# Revit family: ACM_57.71_Volume Control Damper_TVJ
name_source: partatom
category: Duct Accessories
revit_build: Autodesk Revit 2017 (Build: 20170816_0615(x64)
units: mm (PartAtom-declared; Revit-internal decimal feet)

## family parameters
Always vertical = Yes
Cut with Voids When Loaded = No
Part Type = Damper
Round Connector Dimension = Use Diameter
Shared = No
Work Plane-Based = No

## types (49) — shared parameters
ACM_MEP_Air Flow_Max = 0.0 L/s
ACM_MEP_Air Flow_Min = 0.0 L/s
ACM_MEP_Apparent Power = 0 VA
ACM_MEP_Elec. Frecuency = 0 Hz
ACM_MEP_Elec. Power = 0 W
ACM_MEP_Item Type = VCD
ACM_MEP_Number of Poles = 1
ACM_MEP_Pressure_Exhaust = 0.0 Pa
ACM_MEP_Pressure_Max = 0.0 Pa
ACM_MEP_Pressure_Min = 0.0 Pa
ACM_MEP_Pressure_Supply = 0.0 Pa
ACM_MEP_Velocity_Max = 0.0 m/s
ACM_MEP_Velocity_Min = 0.0 m/s
ACM_MEP_Voltage = 0 V
ACM_MEP_Weight = 0.00 kg
CAT0 = Yes
Description = VAV control units, supply/extract air, acoustic cladding
L = 400 mm  [stored 1.31234 ft]
L2 = 200 mm  [stored 0.656168 ft]
L2D = 400 mm  [stored 1.31234 ft]
Manufacturer = TROX
magiPartTypeId = 203
magiProductFamilyId = TVJD-*/*X*
zero-valued in all types: ACM_MEP_Length, ACM_MEP_Motor_Frecuency, ACM_MEP_Power Factor, MC_Default_elevation

## per-type parameters (varying)
| type | ACM_MEP_Connection_Diameter | ACM_MEP_Connection_Height | ACM_MEP_Connection_Width | ACM_MEP_Height | ACM_MEP_Number Type | ACM_MEP_Width | B | B22 | H | H22 | H2D | W2D | magiProductCode | magiProductId |
| 57.71_VCD_Volume Control Damper_TVJ_200X200 | 0 mm  [stored 0 ft] | 0 mm  [stored 0 ft] | 0 mm  [stored 0 ft] | 0 mm  [stored 0 ft] | 200mm x 200mm | 0 mm  [stored 0 ft] | 200 mm | 140 mm  [stored 0.459318 ft] | 200 mm | 140 mm  [stored 0.459318 ft] | 280 mm | 280 mm | TVJ-D/200X200 | TVJD-*/200X200 |
| 57.71_VCD_Volume Control Damper_TVJ_300X100 | 0 mm  [stored 0 ft] | 0 mm  [stored 0 ft] | 0 mm  [stored 0 ft] | 0 mm  [stored 0 ft] |  | 0 mm  [stored 0 ft] | 300 mm | 190 mm  [stored 0.62336 ft] | 100 mm | 90 mm  [stored 0.295276 ft] | 180 mm  [stored 0.590551 ft] | 380 mm | TVJ-D/300X100 | TVJD-*/300X100 |
| 57.71_VCD_Volume Control Damper_TVJ_300X200 | 0 mm  [stored 0 ft] | 0 mm  [stored 0 ft] | 0 mm  [stored 0 ft] | 0 mm  [stored 0 ft] | 300mm x 200mm | 0 mm  [stored 0 ft] | 300 mm | 190 mm  [stored 0.62336 ft] | 200 mm | 140 mm  [stored 0.459318 ft] | 280 mm | 380 mm | TVJ-D/300X200 | TVJD-*/300X200 |
| 57.71_VCD_Volume Control Damper_TVJ_300X300 | 0 mm  [stored 0 ft] | 0 mm  [stored 0 ft] | 0 mm  [stored 0 ft] | 0 mm  [stored 0 ft] | 300mm x 300mm | 0 mm  [stored 0 ft] | 300 mm | 190 mm  [stored 0.62336 ft] | 300 mm | 190 mm  [stored 0.62336 ft] | 380 mm | 380 mm | TVJ-D/300X300 | TVJD-*/300X300 |
| 57.71_VCD_Volume Control Damper_TVJ_400X100 | 0 mm  [stored 0 ft] | 0 mm  [stored 0 ft] | 0 mm  [stored 0 ft] | 0 mm  [stored 0 ft] |  | 0 mm  [stored 0 ft] | 400 mm | 240 mm  [stored 0.787402 ft] | 100 mm | 90 mm  [stored 0.295276 ft] | 180 mm  [stored 0.590551 ft] | 480 mm | TVJ-D/400X100 | TVJD-*/400X100 |
| 57.71_VCD_Volume Control Damper_TVJ_400X200 | 0 mm  [stored 0 ft] | 0 mm  [stored 0 ft] | 0 mm  [stored 0 ft] | 0 mm  [stored 0 ft] |  | 0 mm  [stored 0 ft] | 400 mm | 240 mm  [stored 0.787402 ft] | 200 mm | 140 mm  [stored 0.459318 ft] | 280 mm | 480 mm | TVJ-D/400X200 | TVJD-*/400X200 |
| 57.71_VCD_Volume Control Damper_TVJ_400X300 | 0 mm  [stored 0 ft] | 0 mm  [stored 0 ft] | 0 mm  [stored 0 ft] | 0 mm  [stored 0 ft] | 400mm x 300mm | 0 mm  [stored 0 ft] | 400 mm | 240 mm  [stored 0.787402 ft] | 300 mm | 190 mm  [stored 0.62336 ft] | 380 mm | 480 mm | TVJ-D/400X300 | TVJD-*/400X300 |
| 57.71_VCD_Volume Control Damper_TVJ_400X400 | 0 mm  [stored 0 ft] | 0 mm  [stored 0 ft] | 0 mm  [stored 0 ft] | 0 mm  [stored 0 ft] | 400mm x 400mm | 0 mm  [stored 0 ft] | 400 mm | 240 mm  [stored 0.787402 ft] | 400 mm | 240 mm  [stored 0.787402 ft] | 480 mm | 480 mm | TVJ-D/400X400 | TVJD-*/400X400 |
| 57.71_VCD_Volume Control Damper_TVJ_500X100 | 0 mm  [stored 0 ft] | 0 mm  [stored 0 ft] | 0 mm  [stored 0 ft] | 0 mm  [stored 0 ft] |  | 0 mm  [stored 0 ft] | 500 mm | 290 mm  [stored 0.951444 ft] | 100 mm | 90 mm  [stored 0.295276 ft] | 180 mm  [stored 0.590551 ft] | 580 mm | TVJ-D/500X100 | TVJD-*/500X100 |
| 57.71_VCD_Volume Control Damper_TVJ_500X200 | 0 mm  [stored 0 ft] | 0 mm  [stored 0 ft] | 0 mm  [stored 0 ft] | 0 mm  [stored 0 ft] |  | 0 mm  [stored 0 ft] | 500 mm | 290 mm  [stored 0.951444 ft] | 200 mm | 140 mm  [stored 0.459318 ft] | 280 mm | 580 mm | TVJ-D/500X200 | TVJD-*/500X200 |
| 57.71_VCD_Volume Control Damper_TVJ_500X300 | 0 mm  [stored 0 ft] | 0 mm  [stored 0 ft] | 0 mm  [stored 0 ft] | 0 mm  [stored 0 ft] | 500mm x 300mm | 0 mm  [stored 0 ft] | 500 mm | 290 mm  [stored 0.951444 ft] | 300 mm | 190 mm  [stored 0.62336 ft] | 380 mm | 580 mm | TVJ-D/500X300 | TVJD-*/500X300 |
| 57.71_VCD_Volume Control Damper_TVJ_500X400 | 0 mm  [stored 0 ft] | 0 mm  [stored 0 ft] | 0 mm  [stored 0 ft] | 0 mm  [stored 0 ft] | 500mm x 400mm | 0 mm  [stored 0 ft] | 500 mm | 290 mm  [stored 0.951444 ft] | 400 mm | 240 mm  [stored 0.787402 ft] | 480 mm | 580 mm | TVJ-D/500X400 | TVJD-*/500X400 |
| 57.71_VCD_Volume Control Damper_TVJ_500X500 | 0 mm  [stored 0 ft] | 0 mm  [stored 0 ft] | 0 mm  [stored 0 ft] | 0 mm  [stored 0 ft] |  | 0 mm  [stored 0 ft] | 500 mm | 290 mm  [stored 0.951444 ft] | 500 mm | 290 mm  [stored 0.951444 ft] | 580 mm | 580 mm | TVJ-D/500X500 | TVJD-*/500X500 |
| 57.71_VCD_Volume Control Damper_TVJ_600X100 | 0 mm  [stored 0 ft] | 0 mm  [stored 0 ft] | 0 mm  [stored 0 ft] | 0 mm  [stored 0 ft] |  | 0 mm  [stored 0 ft] | 600 mm | 340 mm  [stored 1.11549 ft] | 100 mm | 90 mm  [stored 0.295276 ft] | 180 mm  [stored 0.590551 ft] | 680 mm | TVJ-D/600X100 | TVJD-*/600X100 |
| 57.71_VCD_Volume Control Damper_TVJ_600X200 | 0 mm  [stored 0 ft] | 0 mm  [stored 0 ft] | 0 mm  [stored 0 ft] | 0 mm  [stored 0 ft] |  | 0 mm  [stored 0 ft] | 600 mm | 340 mm  [stored 1.11549 ft] | 200 mm | 140 mm  [stored 0.459318 ft] | 280 mm | 680 mm | TVJ-D/600X200 | TVJD-*/600X200 |
| 57.71_VCD_Volume Control Damper_TVJ_600X300 | 0 mm  [stored 0 ft] | 0 mm  [stored 0 ft] | 0 mm  [stored 0 ft] | 0 mm  [stored 0 ft] | 600mm x 300mm | 0 mm  [stored 0 ft] | 600 mm | 340 mm  [stored 1.11549 ft] | 300 mm | 190 mm  [stored 0.62336 ft] | 380 mm | 680 mm | TVJ-D/600X300 | TVJD-*/600X300 |
| 57.71_VCD_Volume Control Damper_TVJ_600X400 | 0 mm  [stored 0 ft] | 0 mm  [stored 0 ft] | 0 mm  [stored 0 ft] | 0 mm  [stored 0 ft] | 600mm x 400mm | 0 mm  [stored 0 ft] | 600 mm | 340 mm  [stored 1.11549 ft] | 400 mm | 240 mm  [stored 0.787402 ft] | 480 mm | 680 mm | TVJ-D/600X400 | TVJD-*/600X400 |
| 57.71_VCD_Volume Control Damper_TVJ_600X500 | 0 mm  [stored 0 ft] | 0 mm  [stored 0 ft] | 0 mm  [stored 0 ft] | 0 mm  [stored 0 ft] |  | 0 mm  [stored 0 ft] | 600 mm | 340 mm  [stored 1.11549 ft] | 500 mm | 290 mm  [stored 0.951444 ft] | 580 mm | 680 mm | TVJ-D/600X500 | TVJD-*/600X500 |
| 57.71_VCD_Volume Control Damper_TVJ_600X600 | 0 mm  [stored 0 ft] | 0 mm  [stored 0 ft] | 0 mm  [stored 0 ft] | 0 mm  [stored 0 ft] |  | 0 mm  [stored 0 ft] | 600 mm | 340 mm  [stored 1.11549 ft] | 600 mm | 340 mm  [stored 1.11549 ft] | 680 mm | 680 mm | TVJ-D/600X600 | TVJD-*/600X600 |
| 57.71_VCD_Volume Control Damper_TVJ_700X200 | 0 mm  [stored 0 ft] | 0 mm  [stored 0 ft] | 0 mm  [stored 0 ft] | 0 mm  [stored 0 ft] |  | 0 mm  [stored 0 ft] | 700 mm | 390 mm  [stored 1.27953 ft] | 200 mm | 140 mm  [stored 0.459318 ft] | 280 mm | 780 mm | TVJ-D/700X200 | TVJD-*/700X200 |
| 57.71_VCD_Volume Control Damper_TVJ_700X300 | 0 mm  [stored 0 ft] | 0 mm  [stored 0 ft] | 0 mm  [stored 0 ft] | 0 mm  [stored 0 ft] | 700mm x 300mm | 0 mm  [stored 0 ft] | 700 mm | 390 mm  [stored 1.27953 ft] | 300 mm | 190 mm  [stored 0.62336 ft] | 380 mm | 780 mm | TVJ-D/700X300 | TVJD-*/700X300 |
| 57.71_VCD_Volume Control Damper_TVJ_700X400 | 0 mm  [stored 0 ft] | 0 mm  [stored 0 ft] | 0 mm  [stored 0 ft] | 0 mm  [stored 0 ft] |  | 0 mm  [stored 0 ft] | 700 mm | 390 mm  [stored 1.27953 ft] | 400 mm | 240 mm  [stored 0.787402 ft] | 480 mm | 780 mm | TVJ-D/700X400 | TVJD-*/700X400 |
| 57.71_VCD_Volume Control Damper_TVJ_700X500 | 0 mm  [stored 0 ft] | 0 mm  [stored 0 ft] | 0 mm  [stored 0 ft] | 0 mm  [stored 0 ft] |  | 0 mm  [stored 0 ft] | 700 mm | 390 mm  [stored 1.27953 ft] | 500 mm | 290 mm  [stored 0.951444 ft] | 580 mm | 780 mm | TVJ-D/700X500 | TVJD-*/700X500 |
| 57.71_VCD_Volume Control Damper_TVJ_700X600 | 0 mm  [stored 0 ft] | 0 mm  [stored 0 ft] | 0 mm  [stored 0 ft] | 0 mm  [stored 0 ft] |  | 0 mm  [stored 0 ft] | 700 mm | 390 mm  [stored 1.27953 ft] | 600 mm | 340 mm  [stored 1.11549 ft] | 680 mm | 780 mm | TVJ-D/700X600 | TVJD-*/700X600 |
| 57.71_VCD_Volume Control Damper_TVJ_700X700 | 0 mm  [stored 0 ft] | 0 mm  [stored 0 ft] | 0 mm  [stored 0 ft] | 0 mm  [stored 0 ft] |  | 0 mm  [stored 0 ft] | 700 mm | 390 mm  [stored 1.27953 ft] | 700 mm | 390 mm  [stored 1.27953 ft] | 780 mm | 780 mm | TVJ-D/700X700 | TVJD-*/700X700 |
| 57.71_VCD_Volume Control Damper_TVJ_800X200 | 0 mm  [stored 0 ft] | 0 mm  [stored 0 ft] | 0 mm  [stored 0 ft] | 0 mm  [stored 0 ft] |  | 0 mm  [stored 0 ft] | 800 mm | 440 mm  [stored 1.44357 ft] | 200 mm | 140 mm  [stored 0.459318 ft] | 280 mm | 880 mm | TVJ-D/800X200 | TVJD-*/800X200 |
| 57.71_VCD_Volume Control Damper_TVJ_800X300 | 0 mm  [stored 0 ft] | 0 mm  [stored 0 ft] | 0 mm  [stored 0 ft] | 0 mm  [stored 0 ft] | 800mm x 300mm | 0 mm  [stored 0 ft] | 800 mm | 440 mm  [stored 1.44357 ft] | 300 mm | 190 mm  [stored 0.62336 ft] | 380 mm | 880 mm | TVJ-D/800X300 | TVJD-*/800X300 |
| 57.71_VCD_Volume Control Damper_TVJ_800X400 | 0 mm  [stored 0 ft] | 0 mm  [stored 0 ft] | 0 mm  [stored 0 ft] | 0 mm  [stored 0 ft] |  | 0 mm  [stored 0 ft] | 800 mm | 440 mm  [stored 1.44357 ft] | 400 mm | 240 mm  [stored 0.787402 ft] | 480 mm | 880 mm | TVJ-D/800X400 | TVJD-*/800X400 |
| 57.71_VCD_Volume Control Damper_TVJ_800X500 | 0 mm  [stored 0 ft] | 0 mm  [stored 0 ft] | 0 mm  [stored 0 ft] | 0 mm  [stored 0 ft] |  | 0 mm  [stored 0 ft] | 800 mm | 440 mm  [stored 1.44357 ft] | 500 mm | 290 mm  [stored 0.951444 ft] | 580 mm | 880 mm | TVJ-D/800X500 | TVJD-*/800X500 |
| 57.71_VCD_Volume Control Damper_TVJ_800X600 | 0 mm  [stored 0 ft] | 0 mm  [stored 0 ft] | 0 mm  [stored 0 ft] | 0 mm  [stored 0 ft] |  | 0 mm  [stored 0 ft] | 800 mm | 440 mm  [stored 1.44357 ft] | 600 mm | 340 mm  [stored 1.11549 ft] | 680 mm | 880 mm | TVJ-D/800X600 | TVJD-*/800X600 |
| 57.71_VCD_Volume Control Damper_TVJ_800X700 | 0 mm  [stored 0 ft] | 0 mm  [stored 0 ft] | 0 mm  [stored 0 ft] | 0 mm  [stored 0 ft] |  | 0 mm  [stored 0 ft] | 800 mm | 440 mm  [stored 1.44357 ft] | 700 mm | 390 mm  [stored 1.27953 ft] | 780 mm | 880 mm | TVJ-D/800X700 | TVJD-*/800X700 |
| 57.71_VCD_Volume Control Damper_TVJ_800X800 | 0 mm  [stored 0 ft] | 0 mm  [stored 0 ft] | 0 mm  [stored 0 ft] | 0 mm  [stored 0 ft] |  | 0 mm  [stored 0 ft] | 800 mm | 440 mm  [stored 1.44357 ft] | 800 mm | 440 mm  [stored 1.44357 ft] | 880 mm | 880 mm | TVJ-D/800X800 | TVJD-*/800X800 |
| 57.71_VCD_Volume Control Damper_TVJ_900X300 | 0 mm  [stored 0 ft] | 0 mm  [stored 0 ft] | 0 mm  [stored 0 ft] | 0 mm  [stored 0 ft] |  | 0 mm  [stored 0 ft] | 900 mm | 490 mm  [stored 1.60761 ft] | 300 mm | 190 mm  [stored 0.62336 ft] | 380 mm | 980 mm | TVJ-D/900X300 | TVJD-*/900X300 |
| 57.71_VCD_Volume Control Damper_TVJ_900X400 | 0 mm  [stored 0 ft] | 0 mm  [stored 0 ft] | 0 mm  [stored 0 ft] | 0 mm  [stored 0 ft] |  | 0 mm  [stored 0 ft] | 900 mm | 490 mm  [stored 1.60761 ft] | 400 mm | 240 mm  [stored 0.787402 ft] | 480 mm | 980 mm | TVJ-D/900X400 | TVJD-*/900X400 |
| 57.71_VCD_Volume Control Damper_TVJ_900X500 | 0 mm  [stored 0 ft] | 0 mm  [stored 0 ft] | 0 mm  [stored 0 ft] | 0 mm  [stored 0 ft] |  | 0 mm  [stored 0 ft] | 900 mm | 490 mm  [stored 1.60761 ft] | 500 mm | 290 mm  [stored 0.951444 ft] | 580 mm | 980 mm | TVJ-D/900X500 | TVJD-*/900X500 |
| 57.71_VCD_Volume Control Damper_TVJ_900X600 | 0 mm  [stored 0 ft] | 0 mm  [stored 0 ft] | 0 mm  [stored 0 ft] | 0 mm  [stored 0 ft] |  | 0 mm  [stored 0 ft] | 900 mm | 490 mm  [stored 1.60761 ft] | 600 mm | 340 mm  [stored 1.11549 ft] | 680 mm | 980 mm | TVJ-D/900X600 | TVJD-*/900X600 |
| 57.71_VCD_Volume Control Damper_TVJ_900X700 | 0 mm  [stored 0 ft] | 0 mm  [stored 0 ft] | 0 mm  [stored 0 ft] | 0 mm  [stored 0 ft] |  | 0 mm  [stored 0 ft] | 900 mm | 490 mm  [stored 1.60761 ft] | 700 mm | 390 mm  [stored 1.27953 ft] | 780 mm | 980 mm | TVJ-D/900X700 | TVJD-*/900X700 |
| 57.71_VCD_Volume Control Damper_TVJ_900X800 | 0 mm  [stored 0 ft] | 0 mm  [stored 0 ft] | 0 mm  [stored 0 ft] | 0 mm  [stored 0 ft] |  | 0 mm  [stored 0 ft] | 900 mm | 490 mm  [stored 1.60761 ft] | 800 mm | 440 mm  [stored 1.44357 ft] | 880 mm | 980 mm | TVJ-D/900X800 | TVJD-*/900X800 |
| 57.71_VCD_Volume Control Damper_TVJ_900X900 | 0 mm  [stored 0 ft] | 0 mm  [stored 0 ft] | 0 mm  [stored 0 ft] | 0 mm  [stored 0 ft] |  | 0 mm  [stored 0 ft] | 900 mm | 490 mm  [stored 1.60761 ft] | 900 mm | 490 mm  [stored 1.60761 ft] | 980 mm | 980 mm | TVJ-D/900X900 | TVJD-*/900X900 |
| 57.71_VCD_Volume Control Damper_TVJ_1000X300 | 0 mm  [stored 0 ft] | 0 mm  [stored 0 ft] | 0 mm  [stored 0 ft] | 0 mm  [stored 0 ft] | 1000mm x 300mm | 0 mm  [stored 0 ft] | 1000 mm | 540 mm  [stored 1.77165 ft] | 300 mm | 190 mm  [stored 0.62336 ft] | 380 mm | 1080 mm | TVJ-D/1000X300 | TVJD-*/1000X300 |
| 57.71_VCD_Volume Control Damper_TVJ_1000X400 | 1 mm  [stored 0.00328084 ft] | 2 mm  [stored 0.00656168 ft] | 3 mm  [stored 0.00984252 ft] | 400 mm  [stored 1.31234 ft] | 1000mm x 400mm | 1000 mm  [stored 3.28084 ft] | 1000 mm | 540 mm  [stored 1.77165 ft] | 400 mm | 240 mm  [stored 0.787402 ft] | 480 mm | 1080 mm | TVJ-D/1000X400 | TVJD-*/1000X400 |
| 57.71_VCD_Volume Control Damper_TVJ_1000X500 | 0 mm  [stored 0 ft] | 0 mm  [stored 0 ft] | 0 mm  [stored 0 ft] | 0 mm  [stored 0 ft] |  | 0 mm  [stored 0 ft] | 1000 mm | 540 mm  [stored 1.77165 ft] | 500 mm | 290 mm  [stored 0.951444 ft] | 580 mm | 1080 mm | TVJ-D/1000X500 | TVJD-*/1000X500 |
| 57.71_VCD_Volume Control Damper_TVJ_1000X600 | 0 mm  [stored 0 ft] | 0 mm  [stored 0 ft] | 0 mm  [stored 0 ft] | 0 mm  [stored 0 ft] |  | 0 mm  [stored 0 ft] | 1000 mm | 540 mm  [stored 1.77165 ft] | 600 mm | 340 mm  [stored 1.11549 ft] | 680 mm | 1080 mm | TVJ-D/1000X600 | TVJD-*/1000X600 |
| 57.71_VCD_Volume Control Damper_TVJ_1000X700 | 0 mm  [stored 0 ft] | 0 mm  [stored 0 ft] | 0 mm  [stored 0 ft] | 0 mm  [stored 0 ft] |  | 0 mm  [stored 0 ft] | 1000 mm | 540 mm  [stored 1.77165 ft] | 700 mm | 390 mm  [stored 1.27953 ft] | 780 mm | 1080 mm | TVJ-D/1000X700 | TVJD-*/1000X700 |
| 57.71_VCD_Volume Control Damper_TVJ_1000X800 | 0 mm  [stored 0 ft] | 0 mm  [stored 0 ft] | 0 mm  [stored 0 ft] | 0 mm  [stored 0 ft] |  | 0 mm  [stored 0 ft] | 1000 mm | 540 mm  [stored 1.77165 ft] | 800 mm | 440 mm  [stored 1.44357 ft] | 880 mm | 1080 mm | TVJ-D/1000X800 | TVJD-*/1000X800 |
| 57.71_VCD_Volume Control Damper_TVJ_1000X900 | 0 mm  [stored 0 ft] | 0 mm  [stored 0 ft] | 0 mm  [stored 0 ft] | 0 mm  [stored 0 ft] |  | 0 mm  [stored 0 ft] | 1000 mm | 540 mm  [stored 1.77165 ft] | 900 mm | 490 mm  [stored 1.60761 ft] | 980 mm | 1080 mm | TVJ-D/1000X900 | TVJD-*/1000X900 |
| 57.71_VCD_Volume Control Damper_TVJ_1000X1000 | 0 mm  [stored 0 ft] | 0 mm  [stored 0 ft] | 0 mm  [stored 0 ft] | 0 mm  [stored 0 ft] |  | 0 mm  [stored 0 ft] | 1000 mm | 540 mm  [stored 1.77165 ft] | 1000 mm | 540 mm  [stored 1.77165 ft] | 1080 mm | 1080 mm | TVJ-D/1000X1000 | TVJD-*/1000X1000 |
| 57.71_VCD_Volume Control Damper_TVJ_200X100 | 0 mm  [stored 0 ft] | 0 mm  [stored 0 ft] | 0 mm  [stored 0 ft] | 0 mm  [stored 0 ft] |  | 0 mm  [stored 0 ft] | 200 mm | 140 mm  [stored 0.459318 ft] | 100 mm | 90 mm  [stored 0.295276 ft] | 180 mm  [stored 0.590551 ft] | 280 mm | TVJ-D/200X100 | TVJD-*/200X100 |
| 57.71_VCD_Volume Control Damper_TVJ_1500X400 | 1 mm  [stored 0.00328084 ft] | 2 mm  [stored 0.00656168 ft] | 3 mm  [stored 0.00984252 ft] | 400 mm  [stored 1.31234 ft] | 1500mm x 400mm | 1500 mm  [stored 4.92126 ft] | 1500 mm | 740 mm  [stored 2.42782 ft] | 400 mm | 240 mm  [stored 0.787402 ft] | 480 mm | 1080 mm | TVJ-D/1000X400 | TVJD-*/1000X400 |

note: [stored X ft] marks values corroborated as IEEE doubles in the binary element streams (Revit-internal decimal feet)

## geometry (parser evidence)
native form markers: Blend x2, Sweep x1
no freeform markers — native parametric forms only
